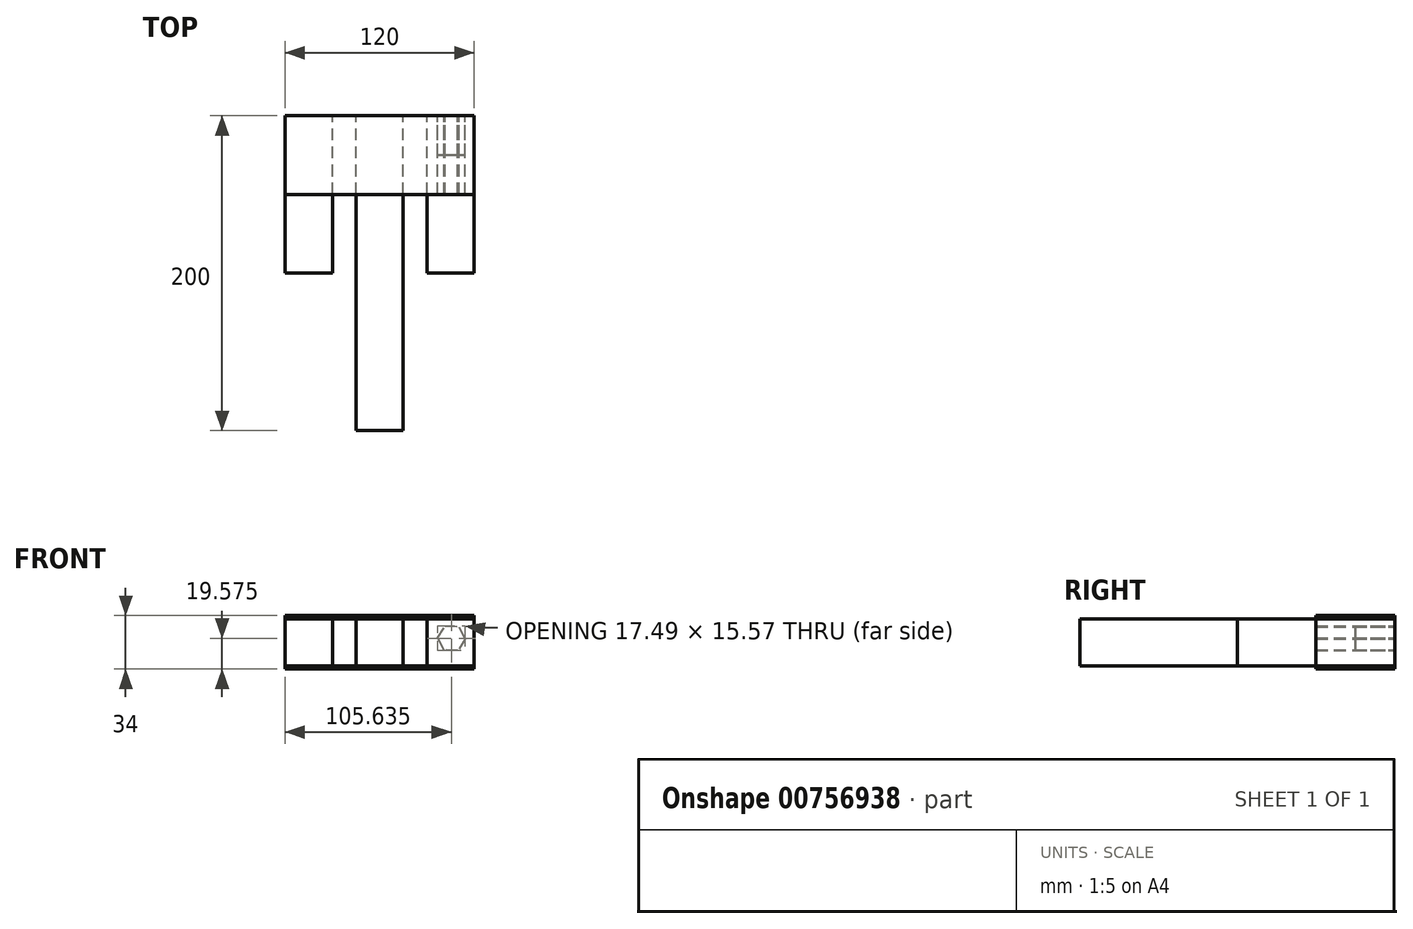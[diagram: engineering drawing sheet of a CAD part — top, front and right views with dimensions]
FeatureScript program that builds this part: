
annotation { "Feature Type Name" : "Feature", "Feature Type Description" : "" }
export const myFeature = defineFeature(function(context is Context, id is Id, definition is map)
    precondition{}
    {
        {
            var Q0;
            Q0=qCreatedBy(makeId("Front.planeOp"),FACE);
            var sketch = newSketch(context, id + "F0", { "sketchPlane" : qUnion([Q0])});
            skLineSegment(sketch, "E0.bottom", {"start": v(-59.57, 4.4) * mm, "end": v(-29.57, 4.4) * mm});
            skLineSegment(sketch, "E0.top", {"start": v(-59.57, -25.6) * mm, "end": v(-29.57, -25.6) * mm});
            skLineSegment(sketch, "E0.left", {"start": v(-59.57, 4.4) * mm, "end": v(-59.57, -25.6) * mm});
            skLineSegment(sketch, "E0.right", {"start": v(-29.57, 4.4) * mm, "end": v(-29.57, -25.6) * mm});
            skLineSegment(sketch, "E1.bottom", {"start": v(-59.57, 4.4) * mm, "end": v(60.43, 4.4) * mm});
            skLineSegment(sketch, "E1.top", {"start": v(-59.57, 6.4) * mm, "end": v(60.43, 6.4) * mm});
            skLineSegment(sketch, "E1.left", {"start": v(-59.57, 4.4) * mm, "end": v(-59.57, 6.4) * mm});
            skLineSegment(sketch, "E1.right", {"start": v(60.43, 4.4) * mm, "end": v(60.43, 6.4) * mm});
            skLineSegment(sketch, "E2.bottom", {"start": v(-59.57, -25.6) * mm, "end": v(60.43, -25.6) * mm});
            skLineSegment(sketch, "E2.top", {"start": v(-59.57, -27.6) * mm, "end": v(60.43, -27.6) * mm});
            skLineSegment(sketch, "E2.left", {"start": v(-59.57, -25.6) * mm, "end": v(-59.57, -27.6) * mm});
            skLineSegment(sketch, "E2.right", {"start": v(60.43, -25.6) * mm, "end": v(60.43, -27.6) * mm});
            skLineSegment(sketch, "E3.bottom", {"start": v(60.43, 4.4) * mm, "end": v(30.43, 4.4) * mm});
            skLineSegment(sketch, "E3.top", {"start": v(60.43, -25.6) * mm, "end": v(30.43, -25.6) * mm});
            skLineSegment(sketch, "E3.left", {"start": v(60.43, 4.4) * mm, "end": v(60.43, -25.6) * mm});
            skLineSegment(sketch, "E3.right", {"start": v(30.43, 4.4) * mm, "end": v(30.43, -25.6) * mm});
            skLineSegment(sketch, "E4.bottom", {"start": v(15.43, -25.6) * mm, "end": v(-14.57, -25.6) * mm});
            skLineSegment(sketch, "E4.top", {"start": v(15.43, 4.4) * mm, "end": v(-14.57, 4.4) * mm});
            skLineSegment(sketch, "E4.left", {"start": v(15.43, -25.6) * mm, "end": v(15.43, 4.4) * mm});
            skLineSegment(sketch, "E4.right", {"start": v(-14.57, -25.6) * mm, "end": v(-14.57, 4.4) * mm});
            skCircle(sketch, "E5.cCircle", {"center": v(46.06, -8.03) * mm, "radius": 7.58 * mm, "construction": true});
            skLineSegment(sketch, "E5.0", {"start": v(41.33, -15.4) * mm, "end": v(37.32, -7.61) * mm});
            skLineSegment(sketch, "E5.1", {"start": v(37.32, -7.61) * mm, "end": v(42.05, -0.24) * mm});
            skLineSegment(sketch, "E5.2", {"start": v(42.05, -0.24) * mm, "end": v(50.8, -0.66) * mm});
            skLineSegment(sketch, "E5.3", {"start": v(50.8, -0.66) * mm, "end": v(54.81, -8.44) * mm});
            skLineSegment(sketch, "E5.4", {"start": v(54.81, -8.44) * mm, "end": v(50.08, -15.8) * mm});
            skLineSegment(sketch, "E5.5", {"start": v(50.08, -15.8) * mm, "end": v(41.33, -15.4) * mm});
            skPoint(sketch, "E5.0.midPoint", {"position": v(39.32, -11.5) * mm});
            skSolve(sketch);
        }
        {
            var Q0;
            Q0 = qSketchRegion(id + "F0", true);
            extrude(context, id + "F1", {"entities" : qUnion([Q0]), "depth" : 50 * mm, "offsetDistance" : 25 * mm});
        }
        {
            var Q0;
            {var subQ2=sQuery(id+"F0.wireOp",EDGE,"E4.left");Q0=makeQuery(id+"F0.imprint","IMPRINT",FACE,{"disambiguationData":[TD([[makeQuery(id+"F0.imprint","IMPRINT",EDGE,{"derivedFrom":subQ2}),1.0]])]});}
            extrude(context, id + "F2", {"entities" : qUnion([Q0]), "operationType" : NewBodyOperationType.ADD, "depth" : 200 * mm, "offsetDistance" : 25 * mm});
        }
        {
            var Q0;
            {var subQ1=sQuery(id+"F0.wireOp",EDGE,"E3.left");Q0=makeQuery(id+"F0.imprint","IMPRINT",FACE,{"disambiguationData":[TD([[makeQuery(id+"F0.imprint","IMPRINT",EDGE,{"derivedFrom":subQ1}),-1.0]])]});}
            var Q1;
            Q1=makeQuery(id+"F0.imprint","IMPRINT",FACE,{"disambiguationData":[TD([[makeQuery(id+"F0.imprint","IMPRINT",EDGE,{"derivedFrom":sQuery(id+"F0.wireOp",EDGE,"E5.0")}),-1.0]])]});
            var Q2;
            Q2=makeQuery(id+"F0.imprint","IMPRINT",FACE,{"disambiguationData":[TD([[makeQuery(id+"F0.imprint","IMPRINT",EDGE,{"derivedFrom":sQuery(id+"F0.wireOp",EDGE,"E0.bottom")}),-1.0]])]});
            extrude(context, id + "F3", {"entities" : qUnion([Q0, Q1, Q2]), "depth" : 100 * mm, "offsetDistance" : 25 * mm});
        }
        {
            var Q0;
            Q0=makeQuery(id+"F0.imprint","IMPRINT",FACE,{"disambiguationData":[TD([[makeQuery(id+"F0.imprint","IMPRINT",EDGE,{"derivedFrom":sQuery(id+"F0.wireOp",EDGE,"E5.0")}),-1.0]])]});
            extrude(context, id + "F4", {"entities" : qUnion([Q0]), "operationType" : NewBodyOperationType.REMOVE, "depth" : 25 * mm, "offsetDistance" : 25 * mm});
        }
    });
